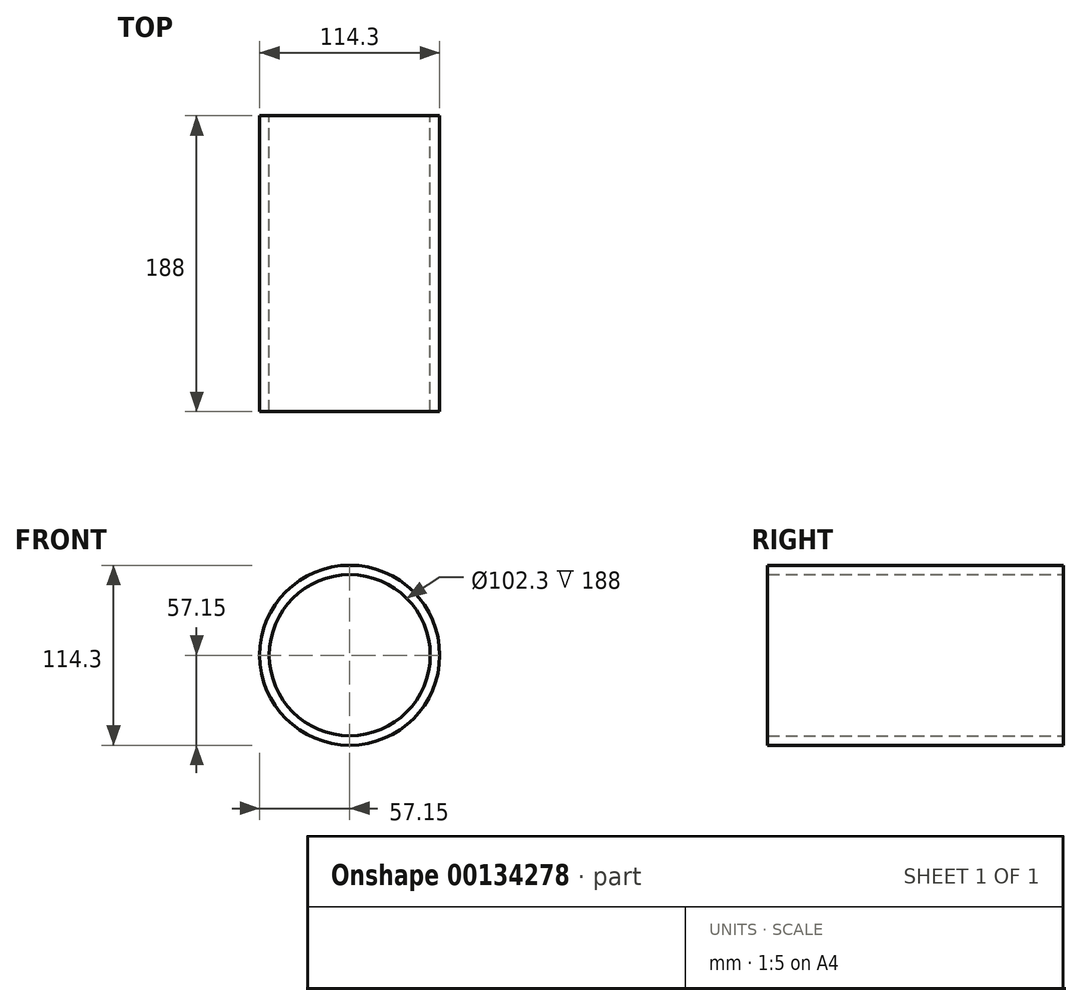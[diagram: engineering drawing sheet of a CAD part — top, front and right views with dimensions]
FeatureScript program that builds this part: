
annotation { "Feature Type Name" : "Feature", "Feature Type Description" : "" }
export const myFeature = defineFeature(function(context is Context, id is Id, definition is map)
    precondition{}
    {
        {
            var Q0;
            Q0=qCreatedBy(makeId("Front.planeOp"),FACE);
            var sketch = newSketch(context, id + "F0", { "sketchPlane" : qUnion([Q0])});
            skCircle(sketch, "E0", {"center": v(0, 0) * mm, "radius": 57.15 * mm});
            skSolve(sketch);
        }
        {
            var Q0;
            Q0=qSketchRegion(id+"F0",true);
            extrude(context, id + "F1", {"entities" : qUnion([Q0]), "depth" : 188 * mm});
        }
        {
            var Q0;
            Q0=makeQuery(id+"F1.opExtrude","CAP_FACE",FACE,{"disambiguationData":[OSD([sQuery(id+"F0.wireOp",EDGE,"E0")])],"isStart":false});
            var Q1;
            Q1=makeQuery(id+"F1.opExtrude","CAP_FACE",FACE,{"disambiguationData":[OSD([sQuery(id+"F0.wireOp",EDGE,"E0")])],"isStart":true});
            shell(context, id + "F2", {"entities" : qUnion([Q0, Q1]), "thickness" : 6 * mm});
        }
    });
